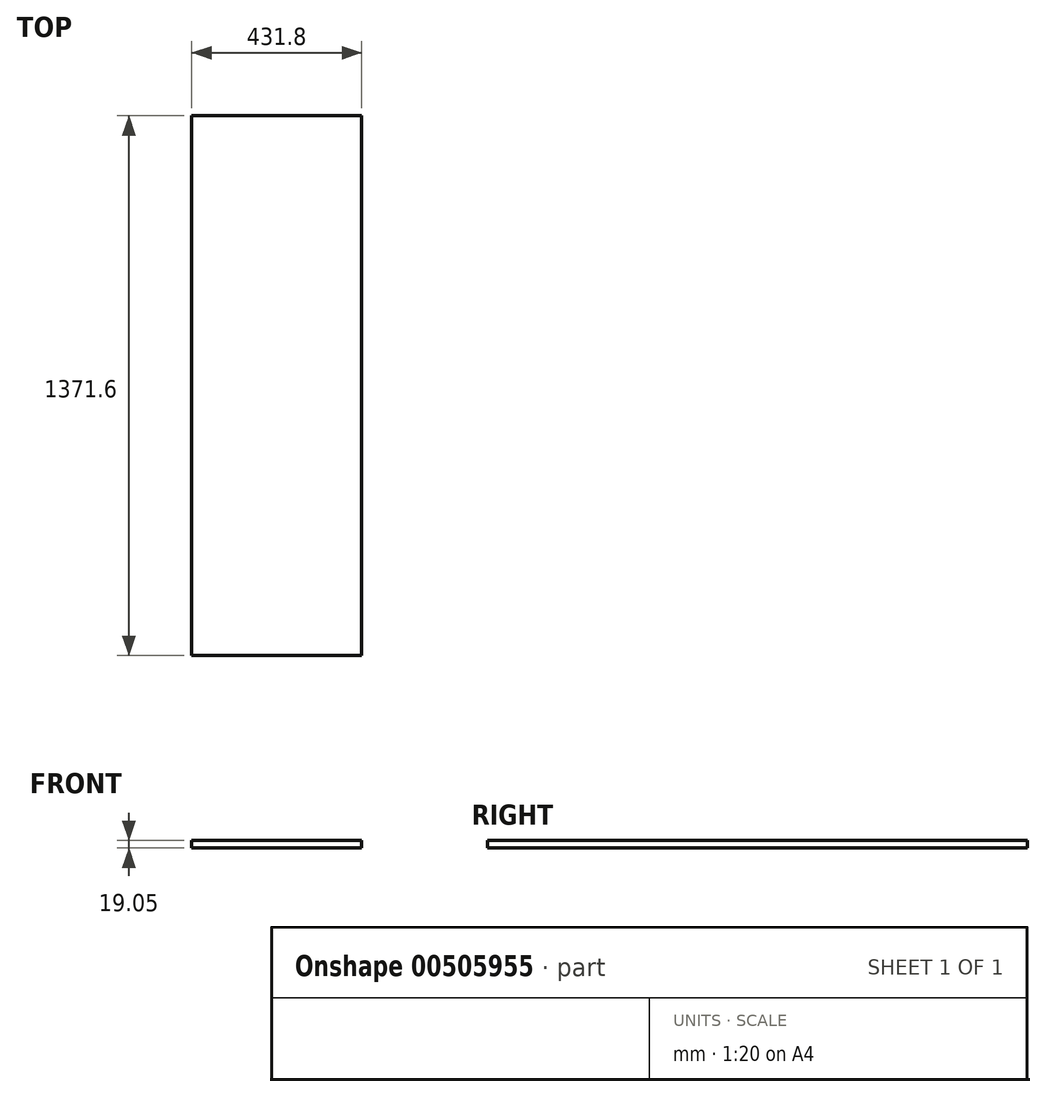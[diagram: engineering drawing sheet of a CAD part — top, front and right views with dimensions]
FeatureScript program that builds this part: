
annotation { "Feature Type Name" : "Feature", "Feature Type Description" : "" }
export const myFeature = defineFeature(function(context is Context, id is Id, definition is map)
    precondition{}
    {
        {
            var Q0;
            Q0=qCreatedBy(makeId("Top.planeOp"),FACE);
            var sketch = newSketch(context, id + "F0", { "sketchPlane" : qUnion([Q0])});
            skLineSegment(sketch, "E0.bottom", {"start": v(-39.06, 1304.51) * mm, "end": v(392.74, 1304.51) * mm});
            skLineSegment(sketch, "E0.top", {"start": v(-39.06, -67.09) * mm, "end": v(392.74, -67.09) * mm});
            skLineSegment(sketch, "E0.left", {"start": v(-39.06, 1304.51) * mm, "end": v(-39.06, -67.09) * mm});
            skLineSegment(sketch, "E0.right", {"start": v(392.74, 1304.51) * mm, "end": v(392.74, -67.09) * mm});
            skSolve(sketch);
        }
        {
            var Q0;
            Q0=makeQuery(id+"F0.imprint","IMPRINT",FACE,{"disambiguationData":[TD([[makeQuery(id+"F0.imprint","IMPRINT",EDGE,{"derivedFrom":sQuery(id+"F0.wireOp",EDGE,"E0.bottom")}),-1.0]])]});
            extrude(context, id + "F1", {"entities" : qUnion([Q0]), "depth" : 19.05 * mm, "offsetDistance" : 25.4 * mm});
        }
    });
